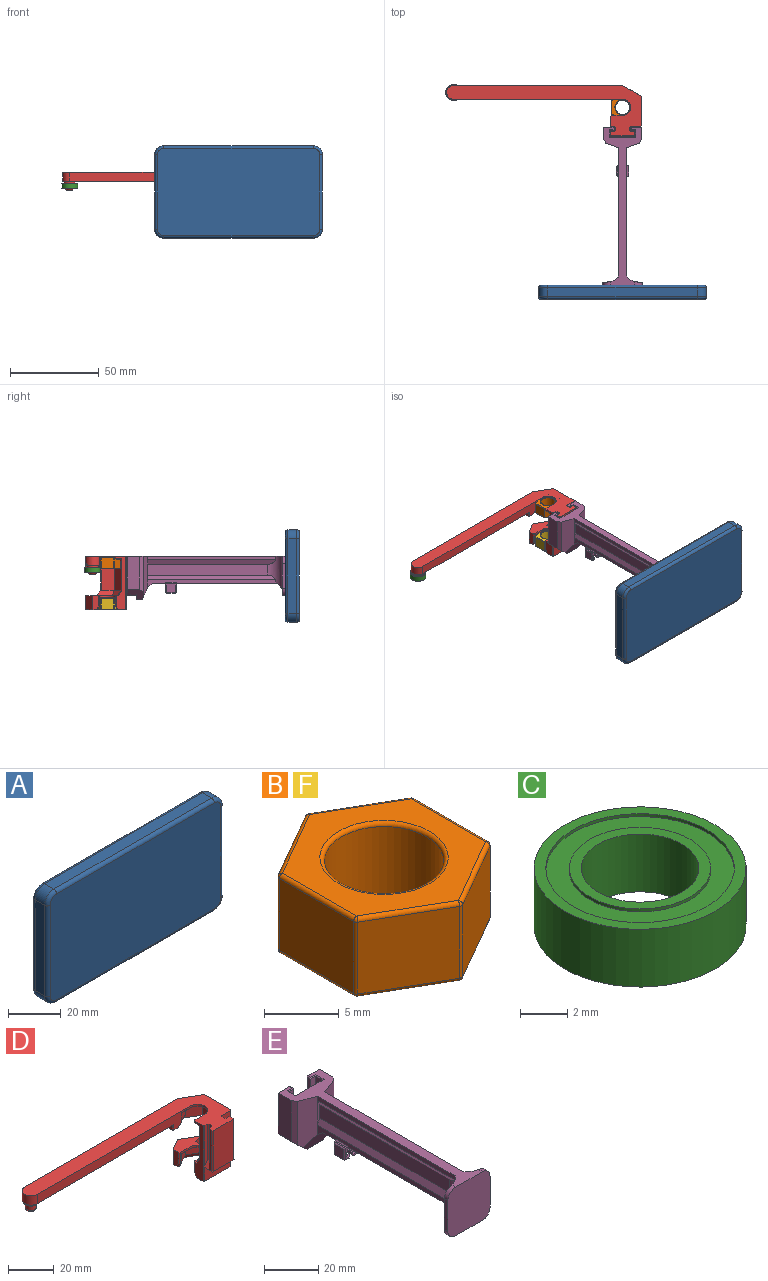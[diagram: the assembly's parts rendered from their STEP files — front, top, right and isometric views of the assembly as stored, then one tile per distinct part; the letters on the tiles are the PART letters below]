
ASSEMBLY  parts=6 mates=3
PART A: 26 faces, bbox 95.2x8x52.8 mm
  f0: plane 84.38x5mm, normal (0,0,-1), area 421.9mm2, adj f6,f9,f15,f24
  f1: plane 41.96x5mm, normal (1,0,0), area 209.8mm2, adj f6,f7,f16,f23
  f2: plane 84.38x5mm, normal (0,0,1), area 421.9mm2, adj f7,f8,f12,f19
  f3: plane 41.96x5mm, normal (-1,0,0), area 209.8mm2, adj f8,f9,f11,f20
  f4: plane 91.38x48.96mm, normal (0,-1,0), area 4463.7mm2, adj f10,f11,f12,f13,f14,f15,f16,f17
  f5: plane 91.38x48.96mm, normal (0,1,0), area 4463.7mm2, adj f18,f19,f20,f21,f22,f23,f24,f25
  f6: cylinder r=5mm len=5mm, axis (0,-1,0), area 39.3mm2, adj f0,f1,f17,f25
  f7: cylinder r=5mm len=5mm, axis (0,1,0), area 39.3mm2, adj f1,f2,f14,f21
  f8: cylinder r=5mm len=5mm, axis (0,-1,0), area 39.3mm2, adj f2,f3,f10,f18
  f9: cylinder r=5mm len=5mm, axis (0,1,0), area 39.3mm2, adj f0,f3,f13,f22
  f10: torus R=3.5mm, axis (0,-1,0), area 16.5mm2, adj f4,f8,f11,f12
  f11: cylinder r=1.5mm len=41.96mm, axis (0,0,1), area 98.9mm2, adj f3,f4,f10,f13
  f12: cylinder r=1.5mm len=84.38mm, axis (1,0,0), area 198.8mm2, adj f2,f4,f10,f14
  f13: torus R=3.5mm, axis (0,-1,0), area 16.5mm2, adj f4,f9,f11,f15
  f14: torus R=3.5mm, axis (0,-1,0), area 16.5mm2, adj f4,f7,f12,f16
  f15: cylinder r=1.5mm len=84.38mm, axis (-1,0,0), area 198.8mm2, adj f0,f4,f13,f17
  f16: cylinder r=1.5mm len=41.96mm, axis (0,0,-1), area 98.9mm2, adj f1,f4,f14,f17
  f17: torus R=3.5mm, axis (0,-1,0), area 16.5mm2, adj f4,f6,f15,f16
  f18: torus R=3.5mm, axis (0,-1,0), area 16.5mm2, adj f5,f8,f19,f20
  f19: cylinder r=1.5mm len=84.38mm, axis (-1,0,0), area 198.8mm2, adj f2,f5,f18,f21
  f20: cylinder r=1.5mm len=41.96mm, axis (0,0,-1), area 98.9mm2, adj f3,f5,f18,f22
  f21: torus R=3.5mm, axis (0,-1,0), area 16.5mm2, adj f5,f7,f19,f23
  f22: torus R=3.5mm, axis (0,-1,0), area 16.5mm2, adj f5,f9,f20,f24
  f23: cylinder r=1.5mm len=41.96mm, axis (0,0,1), area 98.9mm2, adj f1,f5,f21,f25
  f24: cylinder r=1.5mm len=84.38mm, axis (1,0,0), area 198.8mm2, adj f0,f5,f22,f25
  f25: torus R=3.5mm, axis (0,-1,0), area 16.5mm2, adj f5,f6,f23,f24
PART B: 41 faces, bbox 12.8x14.7x6.5 mm
  f0: plane 6.1x5.9mm, normal (0.5,0.87,0), area 41.6mm2, adj f27,f32,f35,f38
  f1: plane 6.1x5.9mm, normal (-0.5,0.87,0), area 41.6mm2, adj f24,f33,f34,f38
  f2: plane 7.04x5.9mm, normal (-1,0,0), area 41.6mm2, adj f14,f23,f24,f25
  f3: plane 6.1x5.9mm, normal (-0.5,-0.87,0), area 41.6mm2, adj f9,f13,f14,f15
  f4: plane 6.1x5.9mm, normal (0.5,-0.87,0), area 41.6mm2, adj f9,f12,f16,f17
  f5: plane 7.04x5.9mm, normal (1,0,0), area 41.6mm2, adj f17,f22,f26,f27
  f6: cylinder r=4mm len=8mm, axis (0,0,-1), area 148.3mm2, adj f39,f40
  f7: plane 14.09x12.2mm, normal (0,0,1), area 70.8mm2, adj f12,f13,f22,f23,f32,f33,f40
  f8: plane 14.09x12.2mm, normal (0,0,-1), area 70.8mm2, adj f15,f16,f25,f26,f34,f35,f39
  f9: cylinder r=0.3mm len=5.9mm, axis (0,0,-1), area 1.9mm2, adj f3,f4,f10,f11
  f10: sphere r=0.3mm, area 0.1mm2, adj f9,f12,f13
  f11: sphere r=0.3mm, area 0.1mm2, adj f9,f15,f16
  f12: cylinder r=0.3mm len=6.25mm, axis (-0.87,-0.5,0), area 3.3mm2, adj f4,f7,f10,f18
  f13: cylinder r=0.3mm len=6.25mm, axis (-0.87,0.5,0), area 3.3mm2, adj f3,f7,f10,f19
  f14: cylinder r=0.3mm len=5.9mm, axis (0,0,-1), area 1.9mm2, adj f2,f3,f19,f20
  f15: cylinder r=0.3mm len=6.25mm, axis (0.87,-0.5,0), area 3.3mm2, adj f3,f8,f11,f20
  f16: cylinder r=0.3mm len=6.25mm, axis (0.87,0.5,0), area 3.3mm2, adj f4,f8,f11,f21
  f17: cylinder r=0.3mm len=5.9mm, axis (0,0,-1), area 1.9mm2, adj f4,f5,f18,f21
  f18: sphere r=0.3mm, area 0.1mm2, adj f12,f17,f22
  f19: sphere r=0.3mm, area 0.1mm2, adj f13,f14,f23
  f20: sphere r=0.3mm, area 0.1mm2, adj f14,f15,f25
  f21: sphere r=0.3mm, area 0.1mm2, adj f16,f17,f26
  f22: cylinder r=0.3mm len=7.04mm, axis (0,-1,0), area 3.3mm2, adj f5,f7,f18,f28
  f23: cylinder r=0.3mm len=7.04mm, axis (0,1,0), area 3.3mm2, adj f2,f7,f19,f29
  f24: cylinder r=0.3mm len=5.9mm, axis (0,0,-1), area 1.9mm2, adj f1,f2,f29,f30
  f25: cylinder r=0.3mm len=7.04mm, axis (0,-1,0), area 3.3mm2, adj f2,f8,f20,f30
  f26: cylinder r=0.3mm len=7.04mm, axis (0,1,0), area 3.3mm2, adj f5,f8,f21,f31
  f27: cylinder r=0.3mm len=5.9mm, axis (0,0,-1), area 1.9mm2, adj f0,f5,f28,f31
  f28: sphere r=0.3mm, area 0.1mm2, adj f22,f27,f32
  f29: sphere r=0.3mm, area 0.1mm2, adj f23,f24,f33
  f30: sphere r=0.3mm, area 0.1mm2, adj f24,f25,f34
  f31: sphere r=0.3mm, area 0.1mm2, adj f26,f27,f35
  f32: cylinder r=0.3mm len=6.25mm, axis (0.87,-0.5,0), area 3.3mm2, adj f0,f7,f28,f36
  f33: cylinder r=0.3mm len=6.25mm, axis (0.87,0.5,0), area 3.3mm2, adj f1,f7,f29,f36
  f34: cylinder r=0.3mm len=6.25mm, axis (-0.87,-0.5,0), area 3.3mm2, adj f1,f8,f30,f37
  f35: cylinder r=0.3mm len=6.25mm, axis (-0.87,0.5,0), area 3.3mm2, adj f0,f8,f31,f37
  f36: sphere r=0.3mm, area 0.1mm2, adj f32,f33,f38
  f37: sphere r=0.3mm, area 0.1mm2, adj f34,f35,f38
  f38: cylinder r=0.3mm len=5.9mm, axis (0,0,-1), area 1.9mm2, adj f0,f1,f36,f37
  f39: torus R=4.3mm, axis (0,0,1), area 12.2mm2, adj f6,f8
  f40: torus R=4.3mm, axis (0,0,1), area 12.2mm2, adj f6,f7
PART C: 12 faces, bbox 9x9x3 mm
  f0: plane 8x8mm, normal (0,0,1), area 22mm2, adj f3,f9
  f1: plane 8x8mm, normal (0,0,-1), area 22mm2, adj f2,f7
  f2: cylinder r=4mm len=8mm, axis (0,0,-1), area 3.8mm2, adj f1,f6
  f3: cylinder r=4mm len=8mm, axis (0,0,-1), area 3.8mm2, adj f0,f5
  f4: cylinder r=4.5mm len=9mm, axis (0,0,-1), area 84.8mm2, adj f5,f6
  f5: plane 9x9mm, normal (0,0,1), area 13.4mm2, adj f3,f4
  f6: plane 9x9mm, normal (0,0,-1), area 13.4mm2, adj f2,f4
  f7: cylinder r=3mm len=6mm, axis (0,0,-1), area 2.8mm2, adj f1,f11
  f8: cylinder r=2.5mm len=5mm, axis (0,0,-1), area 47.1mm2, adj f10,f11
  f9: cylinder r=3mm len=6mm, axis (0,0,-1), area 2.8mm2, adj f0,f10
  f10: plane 6x6mm, normal (0,0,1), area 8.6mm2, adj f8,f9
  f11: plane 6x6mm, normal (0,0,-1), area 8.6mm2, adj f7,f8
PART D: 102 faces, bbox 109.6x28.3x30 mm
  f0: plane 30x16.3mm, normal (0,-1,0), area 252mm2, adj f1,f8,f62,f79,f80,f84,f93
  f1: plane 22.76x17.3mm, normal (0,0,-1), area 156.5mm2, adj f0,f3,f4,f23,f24,f25,f34,f35
  f2: plane 22x13.28mm, normal (0,-1,0), area 269.7mm2, adj f5,f6,f8,f62,f86,f87
  f3: plane 30x16.26mm, normal (1,0,0), area 448.7mm2, adj f1,f8,f11,f18,f29,f84,f90,f91
  f4: plane 30x5.11mm, normal (-1,0,0), area 88mm2, adj f1,f8,f29,f66,f67,f68,f69,f93
  f5: plane 5.91x3mm, normal (-0.74,0,0.67), area 11.2mm2, adj f2,f42,f43,f44,f48,f62,f81,f82
  f6: plane 4.92x3mm, normal (0.74,0,0.67), area 9.2mm2, adj f2,f45,f46,f47,f62,f80,f83,f85
  f7: plane 7.3x5mm, normal (-1,0,0), area 13.5mm2, adj f18,f53,f55,f61,f89,f101
  f8: plane 109.64x28.32mm, normal (0,0,1), area 1042.1mm2, adj f0,f2,f3,f4,f11,f17,f19,f20
  f9: plane 17.5x6.65mm, normal (-0.5,0.87,0), area 134.4mm2, adj f10,f12,f21,f50
  f10: plane 17.5x7.68mm, normal (-1,0,0), area 128.9mm2, adj f9,f15,f18,f21,f51,f92
  f11: plane 10.65x8mm, normal (0.5,0.87,0), area 98.4mm2, adj f3,f8,f18,f55
  f12: plane 17.5x6.15mm, normal (0,1,0), area 107.6mm2, adj f9,f21,f49,f67
  f13: plane 6.65x4.72mm, normal (-0.5,0.87,0), area 34.6mm2, adj f14,f31,f33,f38,f76,f78
  f14: plane 7.68x4.72mm, normal (-1,0,0), area 34.6mm2, adj f13,f28,f33,f37,f77,f78
  f15: plane 7.34x6.5mm, normal (-0.5,-0.87,0), area 50.5mm2, adj f10,f16,f18,f21,f74
  f16: plane 5.62x5.51mm, normal (0.5,-0.87,0), area 29mm2, adj f15,f17,f21,f41,f73,f74
  f17: plane 95.09x8mm, normal (0,-1,0), area 465.4mm2, adj f8,f16,f18,f20,f41,f53,f54,f73
  f18: plane 21.3x8.96mm, normal (0,0,-1), area 79.4mm2, adj f3,f7,f10,f11,f15,f17,f22,f41
  f19: plane 6.15x1mm, normal (0,1,0), area 6.2mm2, adj f8,f20,f69,f71
  f20: cylinder r=4.5mm len=9mm, axis (0,0,1), area 14.1mm2, adj f8,f17,f19,f72
  f21: plane 15.36x12.8mm, normal (0,0,-1), area 60mm2, adj f9,f10,f12,f15,f16,f68,f71,f72
  f22: plane 11x3mm, normal (0,1,0), area 33mm2, adj f18,f52,f90,f92
  f23: plane 10.15x8mm, normal (0.5,0.87,0), area 93.8mm2, adj f1,f29,f96,f97
  f24: plane 8x6.15mm, normal (-0.5,0.87,0), area 56.8mm2, adj f1,f29,f97,f98
  f25: plane 8x3.17mm, normal (-1,0,0), area 24.2mm2, adj f1,f29,f98,f99,f100
  f26: plane 6.15x6mm, normal (0,-1,0), area 9.4mm2, adj f27,f29,f32,f34,f63,f99
  f27: plane 5.51x5.22mm, normal (0.5,-0.87,0), area 28.9mm2, adj f26,f28,f33,f35,f63,f75
  f28: plane 6.65x4.72mm, normal (-0.5,-0.87,0), area 34.6mm2, adj f14,f27,f33,f36,f75,f77
  f29: plane 18.43x17.3mm, normal (0,0,1), area 96.9mm2, adj f3,f4,f23,f24,f25,f26,f30,f32
  f30: plane 6.15x6mm, normal (0,1,0), area 9.4mm2, adj f29,f31,f32,f40,f65,f94
  f31: plane 5.51x5.22mm, normal (0.5,0.87,0), area 28.9mm2, adj f13,f30,f33,f39,f65,f76
  f32: cylinder r=4.5mm len=9mm, axis (0,0,1), area 14.1mm2, adj f26,f29,f30,f64
  f33: plane 15.36x11.29mm, normal (0,0,-1), area 49.8mm2, adj f13,f14,f27,f28,f31,f63,f64,f65
  f34: plane 2x1mm, normal (0,-0.89,-0.45), area 1.1mm2, adj f1,f26,f35,f100
  f35: plane 5.55x4.2mm, normal (0.45,-0.77,-0.45), area 14mm2, adj f1,f27,f34,f75
  f36: plane 7.2x4.74mm, normal (-0.45,-0.77,-0.45), area 17.3mm2, adj f1,f28,f75,f77
  f37: plane 8.32x2mm, normal (-0.89,0,-0.45), area 17.3mm2, adj f1,f14,f77,f78
  f38: plane 7.2x4.74mm, normal (-0.45,0.77,-0.45), area 17.3mm2, adj f1,f13,f76,f78
  f39: plane 5.55x4.2mm, normal (0.45,0.77,-0.45), area 14mm2, adj f1,f31,f40,f76
  f40: plane 2x1mm, normal (0,0.89,-0.45), area 1.1mm2, adj f1,f30,f39,f95
  f41: plane 7.23x3.6mm, normal (0.45,-0.77,-0.45), area 14.8mm2, adj f16,f17,f18,f74
  f42: plane 21.98x1.71mm, normal (-1,0,0), area 37.6mm2, adj f5,f8,f87,f88
  f43: plane 19x1.71mm, normal (-1,0,0), area 32.5mm2, adj f5,f8,f81,f82
  f44: plane 21.43x1.71mm, normal (0,1,0), area 35mm2, adj f5,f8,f81,f88
  f45: plane 21.98x1.71mm, normal (1,0,0), area 37.6mm2, adj f6,f8,f85,f86
  f46: plane 21.43x1.71mm, normal (0,1,0), area 35mm2, adj f6,f8,f83,f85
  f47: plane 19x1.71mm, normal (1,0,0), area 32.5mm2, adj f6,f8,f79,f83
  f48: plane 21.46x1.74mm, normal (0,-1,0), area 35.6mm2, adj f5,f8,f82,f93
  f49: plane 6.15x3mm, normal (0,0.83,0.55), area 21.2mm2, adj f12,f29,f50,f66
  f50: plane 7.19x4.99mm, normal (-0.42,0.72,0.55), area 24.6mm2, adj f9,f29,f49,f51
  f51: plane 9.68x3.38mm, normal (-0.83,0,0.55), area 29.3mm2, adj f10,f29,f50,f52,f92
  f52: plane 5.5x3.38mm, normal (0,0.83,0.55), area 16.3mm2, adj f22,f29,f51,f91,f92
  f53: plane 88.84x5.8mm, normal (0,0,-1), area 480.5mm2, adj f7,f17,f54,f56,f89,f101
  f54: cylinder r=3.9mm len=7.8mm, axis (0,0,1), area 58.1mm2, adj f8,f17,f53,f55,f101
  f55: plane 95.08x8mm, normal (0,1,0), area 322.4mm2, adj f7,f8,f11,f54,f61,f101
  f56: cylinder r=3.25mm len=6.5mm, axis (0,0,1), area 22mm2, adj f53,f57,f101
  f57: plane 6.5x6.5mm, normal (0,0,-1), area 15.1mm2, adj f56,f58
  f58: cylinder r=2.4mm len=4.8mm, axis (0,0,1), area 45.2mm2, adj f57,f60
  f59: plane 2.8x2.8mm, normal (0,0,-1), area 6.2mm2, adj f60
  f60: torus R=1.4mm, axis (0,0,1), area 20.1mm2, adj f58,f59
  f61: plane 10.65x6.15mm, normal (-0.25,0.43,-0.87), area 37.6mm2, adj f7,f18,f55
  f62: plane 13.95x5.91mm, normal (0,0,-1), area 72.2mm2, adj f0,f2,f5,f6,f80,f93
  f63: plane 5.51x0.5mm, normal (0,-0.71,-0.71), area 3.6mm2, adj f26,f27,f33,f64
  f64: cone r=5mm half-angle=45deg, axis (0,0,-1), area 10.6mm2, adj f32,f33,f63,f65
  f65: plane 5.51x0.5mm, normal (0,0.71,-0.71), area 3.6mm2, adj f30,f31,f33,f64
  f66: plane 3x2.5mm, normal (-0.71,0.59,0.39), area 2.5mm2, adj f4,f29,f49,f67
  f67: plane 18.15x0.5mm, normal (-0.71,0.71,0), area 12.6mm2, adj f4,f12,f66,f68
  f68: plane 3.18x0.5mm, normal (-0.71,0,-0.71), area 2.1mm2, adj f4,f21,f67,f70
  f69: plane 1x0.5mm, normal (-0.71,0.71,0), area 0.7mm2, adj f4,f8,f19,f70
  f70: plane 0.5x0.5mm, normal (-0.58,0.58,-0.58), area 0.2mm2, adj f68,f69,f71
  f71: plane 6.15x0.5mm, normal (0,0.71,-0.71), area 4.3mm2, adj f19,f21,f70,f72
  f72: cone r=5mm half-angle=45deg, axis (0,0,-1), area 10.6mm2, adj f20,f21,f71,f73
  f73: plane 5.51x0.5mm, normal (0,-0.71,-0.71), area 3.6mm2, adj f16,f17,f21,f72
  f74: plane 2x1.28mm, normal (-0.03,-0.96,-0.26), area 1mm2, adj f15,f16,f18,f41
  f75: plane 2x1.15mm, normal (0,-0.87,-0.5), area 1mm2, adj f1,f27,f28,f35,f36
  f76: plane 2x1.15mm, normal (0,0.87,-0.5), area 1mm2, adj f1,f13,f31,f38,f39
  f77: plane 2x1.22mm, normal (-0.75,-0.43,-0.5), area 1mm2, adj f1,f14,f28,f36,f37
  f78: plane 2x1.22mm, normal (-0.75,0.43,-0.5), area 1mm2, adj f1,f13,f14,f37,f38
  f79: plane 19x0.5mm, normal (0.71,-0.71,0), area 13.4mm2, adj f0,f8,f47,f80
  f80: plane 3.4x3.19mm, normal (0.52,-0.71,0.48), area 3mm2, adj f0,f6,f62,f79
  f81: plane 19.55x0.5mm, normal (-0.71,0.71,0), area 13.6mm2, adj f5,f8,f43,f44
  f82: plane 19.55x0.5mm, normal (-0.71,-0.71,0), area 13.6mm2, adj f5,f8,f43,f48
  f83: plane 19.55x0.5mm, normal (0.71,0.71,0), area 13.6mm2, adj f6,f8,f46,f47
  f84: plane 30x0.5mm, normal (0.71,-0.71,0), area 21.2mm2, adj f0,f1,f3,f8
  f85: plane 21.98x0.5mm, normal (0.71,0.71,0), area 15.3mm2, adj f6,f8,f45,f46
  f86: plane 21.98x0.5mm, normal (0.71,-0.71,0), area 15.3mm2, adj f2,f6,f8,f45
  f87: plane 21.98x0.5mm, normal (-0.71,-0.71,0), area 15.3mm2, adj f2,f5,f8,f42
  f88: plane 21.98x0.5mm, normal (-0.71,0.71,0), area 15.3mm2, adj f5,f8,f42,f44
  f89: plane 3x0.5mm, normal (-0.71,-0.71,0), area 2.1mm2, adj f7,f17,f18,f53
  f90: plane 11.15x0.5mm, normal (0.71,0.71,0), area 7.8mm2, adj f3,f18,f22,f91
  f91: plane 3x2.5mm, normal (0.71,0.59,0.39), area 2.5mm2, adj f3,f29,f52,f90
  f92: plane 11x0.5mm, normal (-0.71,0.71,0), area 7.6mm2, adj f10,f18,f22,f51,f52
  f93: plane 30x0.5mm, normal (-0.71,-0.71,0), area 21mm2, adj f0,f1,f4,f5,f8,f48,f62
  f94: plane 6x0.5mm, normal (-0.71,0.71,0), area 4.2mm2, adj f4,f29,f30,f95
  f95: plane 2.12x1.56mm, normal (-0.71,0.63,-0.32), area 1.6mm2, adj f1,f4,f40,f94
  f96: plane 8x0.43mm, normal (0.87,0.5,0), area 4mm2, adj f1,f3,f23,f29
  f97: plane 8x0.5mm, normal (0,1,0), area 4mm2, adj f1,f23,f24,f29
  f98: plane 8x0.43mm, normal (-0.87,0.5,0), area 4mm2, adj f1,f24,f25,f29
  f99: plane 6x0.5mm, normal (-0.71,-0.71,0), area 4.2mm2, adj f25,f26,f29,f100
  f100: plane 2.12x1.56mm, normal (-0.71,-0.63,-0.32), area 1.6mm2, adj f1,f25,f34,f99
  f101: cylinder r=2mm len=87.85mm, axis (-1,0,0), area 265.3mm2, adj f7,f53,f54,f55,f56
PART E: 121 faces, bbox 22x89x24.5 mm
  f0: plane 6.2x5.8mm, normal (0,1,0), area 14mm2, adj f3,f5,f7,f45,f47,f65,f70,f75
  f1: plane 6.2x5.8mm, normal (0,-1,0), area 14mm2, adj f2,f3,f5,f45,f47,f68,f73,f78
  f2: plane 57.05x5.58mm, normal (0,0,-1), area 228.9mm2, adj f1,f3,f5,f62,f63,f115
  f3: plane 72.07x4.42mm, normal (-1,0,0), area 139.2mm2, adj f0,f1,f2,f7,f13,f41,f62,f114
  f4: plane 72.07x1.92mm, normal (-1,0,0), area 138.5mm2, adj f10,f13,f40,f62
  f5: plane 72.07x4.42mm, normal (1,0,0), area 139.2mm2, adj f0,f1,f2,f7,f14,f38,f63,f113
  f6: plane 72.07x1.92mm, normal (1,0,0), area 138.5mm2, adj f10,f14,f39,f63
  f7: plane 7x4mm, normal (0,0,-1), area 28mm2, adj f0,f3,f5,f116
  f8: plane 11.16x1.4mm, normal (0,-1,0), area 12mm2, adj f13,f29,f40,f41
  f9: plane 21.83x6.44mm, normal (0,1,0), area 130.2mm2, adj f10,f12,f22,f26,f37,f118
  f10: plane 89.02x21.6mm, normal (0,0,1), area 483.4mm2, adj f4,f6,f9,f11,f12,f13,f14,f15
  f11: plane 21.83x6.44mm, normal (0,1,0), area 130.2mm2, adj f10,f15,f18,f25,f31,f117
  f12: plane 18.5x6.97mm, normal (-1,0,0), area 129mm2, adj f9,f10,f118,f120
  f13: plane 21.68x7.39mm, normal (-0.34,-0.94,0), area 156.6mm2, adj f3,f4,f8,f10,f64,f118,f120
  f14: plane 21.68x7.39mm, normal (0.34,-0.94,0), area 156.6mm2, adj f5,f6,f10,f27,f64,f117,f119
  f15: plane 18.5x6.97mm, normal (1,0,0), area 129mm2, adj f10,f11,f117,f119
  f16: plane 8.2x3.05mm, normal (0,0,-1), area 25mm2, adj f19,f64,f117,f118
  f17: plane 22x22mm, normal (0,-1,0), area 470.3mm2, adj f10,f42,f43,f44,f58,f59,f60,f61
  f18: plane 5.42x3mm, normal (-0.74,0,-0.67), area 7.4mm2, adj f11,f19,f23,f24,f25,f117
  f19: plane 24.1x14.17mm, normal (0,1,0), area 333mm2, adj f16,f18,f21,f23,f26,f34,f117,f118
  f20: plane 21.41x2.71mm, normal (0,-1,0), area 54mm2, adj f21,f22,f26,f36
  f21: plane 21.41x3.61mm, normal (1,0,0), area 77.3mm2, adj f19,f20,f26,f35
  f22: plane 18.43x1.81mm, normal (1,0,0), area 33.4mm2, adj f9,f20,f26,f37
  f23: plane 21.41x3.61mm, normal (-1,0,0), area 77.3mm2, adj f18,f19,f24,f33
  f24: plane 21.41x2.71mm, normal (0,-1,0), area 54mm2, adj f18,f23,f25,f32
  f25: plane 18.43x1.81mm, normal (-1,0,0), area 33.4mm2, adj f11,f18,f24,f31
  f26: plane 5.42x3mm, normal (0.74,0,-0.67), area 7.4mm2, adj f9,f19,f20,f21,f22,f118
  f27: plane 11.16x1.4mm, normal (0,-1,0), area 12mm2, adj f14,f30,f38,f39
  f28: plane 22x21.67mm, normal (0,1,0), area 161mm2, adj f42,f43,f44,f58,f59,f60,f61,f62
  f29: plane 67.55x6mm, normal (-1,0,0), area 405.3mm2, adj f8,f40,f41,f62
  f30: plane 67.55x6mm, normal (1,0,0), area 405.3mm2, adj f27,f38,f39,f63
  f31: plane 1.81x0.4mm, normal (-0.71,0,0.71), area 0.9mm2, adj f10,f11,f25,f32
  f32: plane 3.11x0.4mm, normal (0,-0.71,0.71), area 1.5mm2, adj f10,f24,f31,f33
  f33: plane 4.41x0.4mm, normal (-0.71,0,0.71), area 2.3mm2, adj f10,f23,f32,f34
  f34: plane 14.94x0.4mm, normal (0,0.71,0.71), area 8.2mm2, adj f10,f19,f33,f35
  f35: plane 4.41x0.4mm, normal (0.71,0,0.71), area 2.3mm2, adj f10,f21,f34,f36
  f36: plane 3.11x0.4mm, normal (0,-0.71,0.71), area 1.5mm2, adj f10,f20,f35,f37
  f37: plane 1.81x0.4mm, normal (0.71,0,0.71), area 0.9mm2, adj f9,f10,f22,f36
  f38: plane 72.07x2.58mm, normal (0.88,0,0.48), area 207.2mm2, adj f5,f27,f30,f63
  f39: plane 72.07x2.58mm, normal (0.88,0,-0.48), area 207.2mm2, adj f6,f27,f30,f63
  f40: plane 72.07x2.58mm, normal (-0.88,0,-0.48), area 207.2mm2, adj f4,f8,f29,f62
  f41: plane 72.07x2.58mm, normal (-0.88,0,0.48), area 207.2mm2, adj f3,f8,f29,f62
  f42: plane 14x1.8mm, normal (0,0,-1), area 25.2mm2, adj f17,f28,f59,f61
  f43: plane 14x1.8mm, normal (1,0,0), area 25.2mm2, adj f17,f28,f60,f61
  f44: plane 14x1.8mm, normal (-1,0,0), area 25.2mm2, adj f17,f28,f58,f59
  f45: plane 6x0.6mm, normal (0,0,1), area 3.6mm2, adj f0,f1,f66,f113
  f46: plane 5x4.8mm, normal (1,0,0), area 24mm2, adj f65,f66,f68,f69
  f47: plane 6x0.6mm, normal (0,0,1), area 3.6mm2, adj f0,f1,f90,f114
  f48: plane 5x4.8mm, normal (-1,0,0), area 24mm2, adj f85,f90,f95,f96
  f49: plane 5x1.75mm, normal (0,0,-1), area 8.8mm2, adj f94,f95,f105,f106
  f50: plane 5x1mm, normal (1,0,0), area 5mm2, adj f51,f93,f105,f111
  f51: plane 5x0.75mm, normal (0,0,1), area 3.8mm2, adj f50,f100,f108,f112
  f52: plane 5x1.8mm, normal (1,0,0), area 9mm2, adj f98,f99,f107,f108
  f53: plane 5x3.2mm, normal (0,0,-1), area 16mm2, adj f87,f88,f97,f98
  f54: plane 5x1.8mm, normal (-1,0,0), area 9mm2, adj f81,f82,f86,f87
  f55: plane 5x0.75mm, normal (0,0,1), area 3.8mm2, adj f56,f77,f80,f81
  f56: plane 5x1mm, normal (-1,0,0), area 5mm2, adj f55,f74,f75,f78
  f57: plane 5x1.75mm, normal (0,0,-1), area 8.8mm2, adj f69,f70,f73,f74
  f58: cylinder r=4mm len=4mm, axis (0,1,0), area 11.4mm2, adj f10,f17,f28,f44,f62
  f59: cylinder r=4mm len=4mm, axis (0,1,0), area 11.3mm2, adj f17,f28,f42,f44
  f60: cylinder r=4mm len=4mm, axis (0,-1,0), area 11.4mm2, adj f10,f17,f28,f43,f63
  f61: cylinder r=4mm len=4mm, axis (0,-1,0), area 11.3mm2, adj f17,f28,f42,f43
  f62: cylinder r=8mm len=18mm, axis (0,0,-1), area 166.3mm2, adj f2,f3,f4,f10,f28,f29,f40,f41
  f63: cylinder r=8mm len=18mm, axis (0,0,1), area 166.3mm2, adj f2,f5,f6,f10,f28,f30,f38,f39
  f64: plane 14.5x7mm, normal (0,-0.91,-0.42), area 77.7mm2, adj f13,f14,f16,f116,f117,f118
  f65: plane 5.3x0.5mm, normal (0.71,0.71,0), area 3.6mm2, adj f0,f46,f66,f67
  f66: plane 6x0.5mm, normal (0.71,0,0.71), area 3.9mm2, adj f45,f46,f65,f68
  f67: plane 0.5x0.5mm, normal (0.58,0.58,-0.58), area 0.2mm2, adj f65,f69,f70
  f68: plane 5.3x0.5mm, normal (0.71,-0.71,0), area 3.6mm2, adj f1,f46,f66,f71
  f69: plane 5x0.5mm, normal (0.71,0,-0.71), area 3.5mm2, adj f46,f57,f67,f71
  f70: plane 1.75x0.5mm, normal (0,0.71,-0.71), area 1.2mm2, adj f0,f57,f67,f72
  f71: plane 0.5x0.5mm, normal (0.58,-0.58,-0.58), area 0.2mm2, adj f68,f69,f73
  f72: plane 0.5x0.5mm, normal (-0.58,0.58,-0.58), area 0.2mm2, adj f70,f74,f75
  f73: plane 1.75x0.5mm, normal (0,-0.71,-0.71), area 1.2mm2, adj f1,f57,f71,f76
  f74: plane 5x0.5mm, normal (-0.71,0,-0.71), area 3.5mm2, adj f56,f57,f72,f76
  f75: plane 1x0.5mm, normal (-0.71,0.71,0), area 0.5mm2, adj f0,f56,f72,f77
  f76: plane 0.5x0.5mm, normal (-0.58,-0.58,-0.58), area 0.2mm2, adj f73,f74,f78
  f77: plane 0.75x0.5mm, normal (0,0.71,0.71), area 0.4mm2, adj f0,f55,f75,f79
  f78: plane 1x0.5mm, normal (-0.71,-0.71,0), area 0.5mm2, adj f1,f56,f76,f80
  f79: plane 1x1mm, normal (-0.58,0.58,0.58), area 0.6mm2, adj f0,f77,f81,f82
  f80: plane 0.75x0.5mm, normal (0,-0.71,0.71), area 0.4mm2, adj f1,f55,f78,f83
  f81: plane 5x0.5mm, normal (-0.71,0,0.71), area 3.5mm2, adj f54,f55,f79,f83
  f82: plane 1.8x0.5mm, normal (-0.71,0.71,0), area 1.3mm2, adj f0,f54,f79,f84
  f83: plane 1x1mm, normal (-0.58,-0.58,0.58), area 0.6mm2, adj f1,f80,f81,f86
  f84: plane 1x1mm, normal (-0.58,0.58,-0.58), area 0.6mm2, adj f0,f82,f87,f88
  f85: plane 5.3x0.5mm, normal (-0.71,0.71,0), area 3.6mm2, adj f0,f48,f89,f90
  f86: plane 1.8x0.5mm, normal (-0.71,-0.71,0), area 1.3mm2, adj f1,f54,f83,f91
  f87: plane 5x0.5mm, normal (-0.71,0,-0.71), area 3.5mm2, adj f53,f54,f84,f91
  f88: plane 3.2x0.5mm, normal (0,0.71,-0.71), area 2.3mm2, adj f0,f53,f84,f92
  f89: plane 0.5x0.5mm, normal (-0.58,0.58,-0.58), area 0.2mm2, adj f85,f94,f95
  f90: plane 6x0.5mm, normal (-0.71,0,0.71), area 3.9mm2, adj f47,f48,f85,f96
  f91: plane 1x1mm, normal (-0.58,-0.58,-0.58), area 0.6mm2, adj f1,f86,f87,f97
  f92: plane 1x1mm, normal (0.58,0.58,-0.58), area 0.6mm2, adj f0,f88,f98,f99
  f93: plane 1x0.5mm, normal (0.71,0.71,0), area 0.5mm2, adj f0,f50,f100,f101
  f94: plane 1.75x0.5mm, normal (0,0.71,-0.71), area 1.2mm2, adj f0,f49,f89,f101
  f95: plane 5x0.5mm, normal (-0.71,0,-0.71), area 3.5mm2, adj f48,f49,f89,f102
  f96: plane 5.3x0.5mm, normal (-0.71,-0.71,0), area 3.6mm2, adj f1,f48,f90,f102
  f97: plane 3.2x0.5mm, normal (0,-0.71,-0.71), area 2.3mm2, adj f1,f53,f91,f103
  f98: plane 5x0.5mm, normal (0.71,0,-0.71), area 3.5mm2, adj f52,f53,f92,f103
  f99: plane 1.8x0.5mm, normal (0.71,0.71,0), area 1.3mm2, adj f0,f52,f92,f104
  f100: plane 0.75x0.5mm, normal (0,0.71,0.71), area 0.4mm2, adj f0,f51,f93,f104
  f101: plane 0.5x0.5mm, normal (0.58,0.58,-0.58), area 0.2mm2, adj f93,f94,f105
  f102: plane 0.5x0.5mm, normal (-0.58,-0.58,-0.58), area 0.2mm2, adj f95,f96,f106
  f103: plane 1x1mm, normal (0.58,-0.58,-0.58), area 0.6mm2, adj f1,f97,f98,f107
  f104: plane 1x1mm, normal (0.58,0.58,0.58), area 0.6mm2, adj f0,f99,f100,f108
  f105: plane 5x0.5mm, normal (0.71,0,-0.71), area 3.5mm2, adj f49,f50,f101,f109
  f106: plane 1.75x0.5mm, normal (0,-0.71,-0.71), area 1.2mm2, adj f1,f49,f102,f109
  f107: plane 1.8x0.5mm, normal (0.71,-0.71,0), area 1.3mm2, adj f1,f52,f103,f110
  f108: plane 5x0.5mm, normal (0.71,0,0.71), area 3.5mm2, adj f51,f52,f104,f110
  f109: plane 0.5x0.5mm, normal (0.58,-0.58,-0.58), area 0.2mm2, adj f105,f106,f111
  f110: plane 1x1mm, normal (0.58,-0.58,0.58), area 0.6mm2, adj f1,f107,f108,f112
  f111: plane 1x0.5mm, normal (0.71,-0.71,0), area 0.5mm2, adj f1,f50,f109,f112
  f112: plane 0.75x0.5mm, normal (0,-0.71,0.71), area 0.4mm2, adj f1,f51,f110,f111
  f113: plane 6x0.5mm, normal (0.71,0,0.71), area 4.2mm2, adj f0,f1,f5,f45
  f114: plane 6x0.5mm, normal (-0.71,0,0.71), area 4.2mm2, adj f0,f1,f3,f47
  f115: plane 17.2x3mm, normal (0,0.77,-0.64), area 35.8mm2, adj f2,f28,f62,f63
  f116: plane 4x3mm, normal (0,-0.64,-0.77), area 15.6mm2, adj f3,f5,f7,f64
  f117: plane 9.76x6.7mm, normal (0.67,0,-0.74), area 58.8mm2, adj f11,f14,f15,f16,f18,f19,f64,f119
  f118: plane 9.76x6.7mm, normal (-0.67,0,-0.74), area 58.8mm2, adj f9,f12,f13,f16,f19,f26,f64,f120
  f119: plane 19.76x2.01mm, normal (0.82,-0.57,0), area 47mm2, adj f10,f14,f15,f117
  f120: plane 19.76x2.01mm, normal (-0.82,-0.57,0), area 47mm2, adj f10,f12,f13,f118
PART F: same geometry as B
PLACE A t=(51.18,-21.2,-0.44)mm
PLACE B t=(54.68,78.88,3.56)mm
PLACE C t=(29.7,87.28,3.06)mm
PLACE D t=(-167.52,78.88,10.56)mm
PLACE E t=(51.18,78.8,10.56)mm
PLACE F t=(54.68,78.88,-19.44)mm
MATE fastened C.f2 <-> D.f54  axis (0,0,1) through (-43.91,87.28,4.56)mm
MATE fastened B.f6 <-> D.f20  axis (0,0,1) through (51.18,78.88,10.06)mm
MATE fastened A.f5 <-> E.f17  axis (0,1,0) through (51.18,-21.2,-0.44)mm
